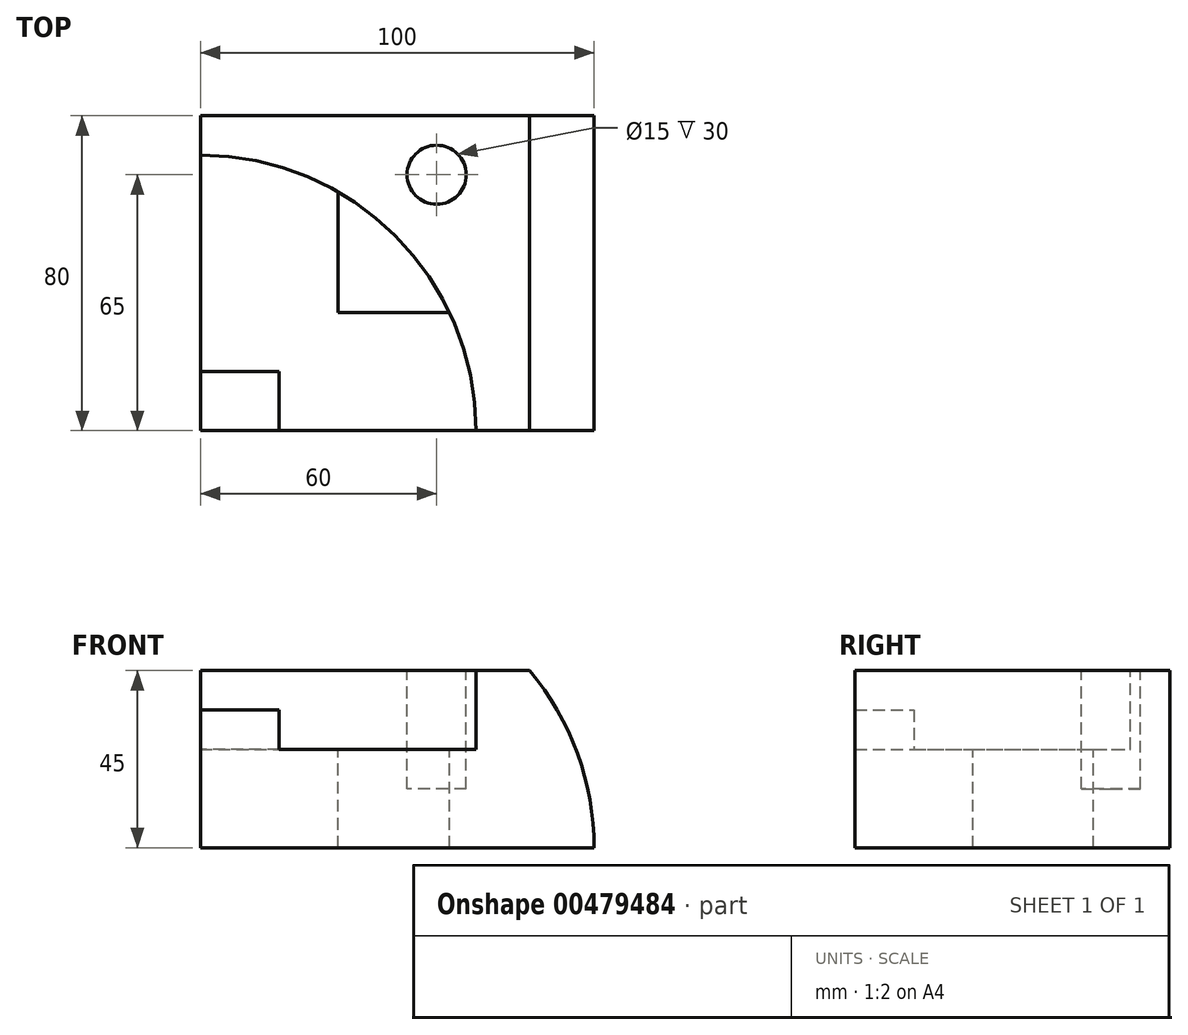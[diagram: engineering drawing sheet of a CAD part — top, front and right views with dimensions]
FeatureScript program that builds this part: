
annotation { "Feature Type Name" : "Feature", "Feature Type Description" : "" }
export const myFeature = defineFeature(function(context is Context, id is Id, definition is map)
    precondition{}
    {
        {
            var Q0;
            Q0=qCreatedBy(makeId("Top.planeOp"),FACE);
            var sketch = newSketch(context, id + "F0", { "sketchPlane" : qUnion([Q0])});
            skLineSegment(sketch, "E0.bottom", {"start": v(0, 0) * mm, "end": v(100, 0) * mm});
            skLineSegment(sketch, "E0.top", {"start": v(0, 80) * mm, "end": v(100, 80) * mm});
            skLineSegment(sketch, "E0.left", {"start": v(0, 0) * mm, "end": v(0, 80) * mm});
            skLineSegment(sketch, "E0.right", {"start": v(100, 0) * mm, "end": v(100, 80) * mm});
            skSolve(sketch);
        }
        {
            var Q0;
            Q0 = qSketchRegion(id + "F0", true);
            extrude(context, id + "F1", {"entities" : qUnion([Q0]), "depth" : 45 * mm});
        }
        {
            var Q0;
            Q0=makeQuery(id+"F1.opExtrude","CAP_FACE",FACE,{"disambiguationData":[OSD([sQuery(id+"F0.wireOp",EDGE,"E0.bottom"),sQuery(id+"F0.wireOp",EDGE,"E0.top"),sQuery(id+"F0.wireOp",EDGE,"E0.left"),sQuery(id+"F0.wireOp",EDGE,"E0.right")])],"isStart":false});
            var sketch = newSketch(context, id + "F2", { "sketchPlane" : qUnion([Q0])});
            skCircle(sketch, "E1", {"center": v(0, 0) * mm, "radius": 70 * mm});
            skSolve(sketch);
        }
        {
            var Q0;
            {var subQ1=sQuery(id+"F2.wireOp",EDGE,"mIytq59y-3JZC-fxpc-JFIN-FHhpayJPknPn.bottom");Q0=makeQuery(id+"F2.imprint","IMPRINT",FACE,{"disambiguationData":[TD([[makeQuery(id+"F2.imprint","IMPRINT",EDGE,{"derivedFrom":subQ1}),-1.0]])]});}
            var Q1;
            {var subQ7=sQuery(id+"F2.wireOp",EDGE,"mIytq59y-3JZC-fxpc-JFIN-FHhpayJPknPn.top");Q1=makeQuery(id+"F2.imprint","IMPRINT",FACE,{"disambiguationData":[TD([[makeQuery(id+"F2.imprint","IMPRINT",EDGE,{"derivedFrom":subQ7}),1.0]])]});}
            var Q2;
            {var subQ0=sQuery(id+"F2.wireOp",EDGE,"E1");var subQ1=makeQuery(id+"F1.opExtrude","CAP_EDGE",EDGE,{"disambiguationData":[OSD([sQuery(id+"F0.wireOp",EDGE,"E0.bottom")])],"isStart":false});var subQ2=makeQuery(id+"F2.imprint","INTERSECT",VERTEX,{"derivedFrom":[subQ1,subQ0]});Q2=makeQuery(id+"F2.imprint","IMPRINT",FACE,{"disambiguationData":[TD([[makeQuery(id+"F2.imprint","IMPRINT",EDGE,{"disambiguationData":[TD([[subQ2,-1.0]])],"derivedFrom":subQ0}),1.0]])]});}
            extrude(context, id + "F3", {"entities" : qUnion([Q0, Q1, Q2]), "operationType" : NewBodyOperationType.REMOVE, "oppositeDirection" : true, "depth" : 20 * mm});
        }
        {
            var Q0;
            Q0=makeQuery(id+"F3.boolean.opBoolean","COPY",FACE,{"derivedFrom":makeQuery(id+"F3.opExtrude","CAP_FACE",FACE,{"disambiguationData":[OSD([sQuery(id+"F0.wireOp",EDGE,"E0.bottom"),sQuery(id+"F0.wireOp",EDGE,"E0.left"),sQuery(id+"F2.wireOp",EDGE,"E1")])],"isStart":false})});
            var sketch = newSketch(context, id + "F4", { "sketchPlane" : qUnion([Q0])});
            skLineSegment(sketch, "E2.bottom", {"start": v(0, 0) * mm, "end": v(20, 0) * mm});
            skLineSegment(sketch, "E2.top", {"start": v(0, 15) * mm, "end": v(20, 15) * mm});
            skLineSegment(sketch, "E2.left", {"start": v(0, 0) * mm, "end": v(0, 15) * mm});
            skLineSegment(sketch, "E2.right", {"start": v(20, 0) * mm, "end": v(20, 15) * mm});
            skSolve(sketch);
        }
        {
            var Q0;
            Q0 = qSketchRegion(id + "F4", true);
            extrude(context, id + "F5", {"entities" : qUnion([Q0]), "operationType" : NewBodyOperationType.ADD, "depth" : 10 * mm});
        }
        {
            var Q0;
            Q0=makeQuery(id+"F3.boolean.opBoolean","COPY",FACE,{"derivedFrom":makeQuery(id+"F3.opExtrude","CAP_FACE",FACE,{"disambiguationData":[OSD([sQuery(id+"F0.wireOp",EDGE,"E0.bottom"),sQuery(id+"F0.wireOp",EDGE,"E0.left"),sQuery(id+"F2.wireOp",EDGE,"E1")])],"isStart":false})});
            var sketch = newSketch(context, id + "F6", { "sketchPlane" : qUnion([Q0])});
            skLineSegment(sketch, "E3", {"start": v(35, 30) * mm, "end": v(35, 60.62) * mm});
            skLineSegment(sketch, "E4", {"start": v(35, 30) * mm, "end": v(63.25, 30) * mm});
            skSolve(sketch);
        }
        {
            var Q0;
            {var subQ0=sQuery(id+"F6.wireOp",EDGE,"E3");Q0=makeQuery(id+"F6.imprint","IMPRINT",FACE,{"disambiguationData":[TD([[makeQuery(id+"F6.imprint","IMPRINT",EDGE,{"derivedFrom":subQ0}),-1.0]])]});}
            extrude(context, id + "F7", {"entities" : qUnion([Q0]), "operationType" : NewBodyOperationType.REMOVE, "endBound" : BoundingType.THROUGH_ALL, "oppositeDirection" : true, "depth" : 25 * mm});
        }
        {
            var Q0;
            Q0=makeQuery(id+"F1.opExtrude","CAP_FACE",FACE,{"disambiguationData":[OSD([sQuery(id+"F0.wireOp",EDGE,"E0.bottom"),sQuery(id+"F0.wireOp",EDGE,"E0.top"),sQuery(id+"F0.wireOp",EDGE,"E0.left"),sQuery(id+"F0.wireOp",EDGE,"E0.right")])],"isStart":false});
            var sketch = newSketch(context, id + "F8", { "sketchPlane" : qUnion([Q0])});
            skCircle(sketch, "E5", {"center": v(60, 65) * mm, "radius": 7.5 * mm});
            skSolve(sketch);
        }
        {
            var Q0;
            Q0 = qSketchRegion(id + "F8", true);
            extrude(context, id + "F9", {"entities" : qUnion([Q0]), "operationType" : NewBodyOperationType.REMOVE, "oppositeDirection" : true, "depth" : 30 * mm});
        }
        {
            var Q0;
            Q0=makeQuery(id+"F5.boolean.opBoolean","MERGE",FACE,{"derivedFrom":[makeQuery(id+"F1.opExtrude","SWEPT_FACE",FACE,{"disambiguationData":[OSD([sQuery(id+"F0.wireOp",EDGE,"E0.bottom")])]}),makeQuery(id+"F5.opExtrude","SWEPT_FACE",FACE,{"disambiguationData":[OSD([sQuery(id+"F4.wireOp",EDGE,"E2.bottom")])]})]});
            var sketch = newSketch(context, id + "F10", { "sketchPlane" : qUnion([Q0])});
            skCircle(sketch, "E6", {"center": v(30, 0) * mm, "radius": 70 * mm});
            skSolve(sketch);
        }
        {
            var Q0;
            {var subQ1=sQuery(id+"F0.wireOp",EDGE,"E0.bottom");var subQ2=makeQuery(id+"F1.opExtrude","SWEPT_EDGE",EDGE,{"disambiguationData":[OSD([subQ1,sQuery(id+"F0.wireOp",EDGE,"E0.right")])]});Q0=makeQuery(id+"F10.imprint","IMPRINT",FACE,{"disambiguationData":[TD([[makeQuery(id+"F10.imprint","IMPRINT",EDGE,{"derivedFrom":subQ2}),-1.0]])]});}
            extrude(context, id + "F11", {"entities" : qUnion([Q0]), "operationType" : NewBodyOperationType.REMOVE, "endBound" : BoundingType.THROUGH_ALL, "oppositeDirection" : true, "depth" : 25 * mm});
        }
    });
